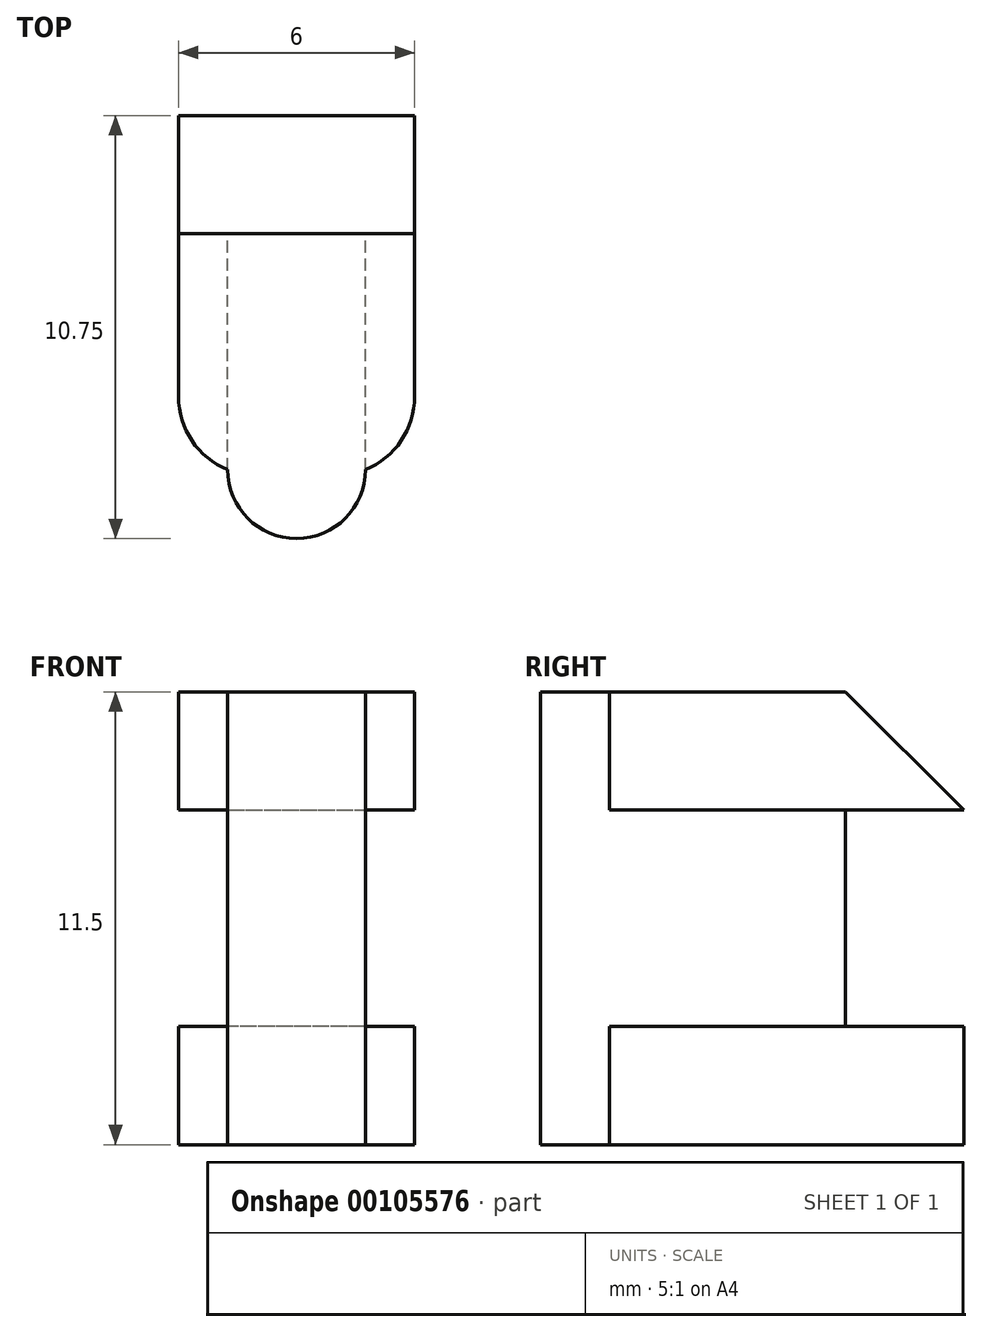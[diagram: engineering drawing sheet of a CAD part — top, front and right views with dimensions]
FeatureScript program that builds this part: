
annotation { "Feature Type Name" : "Feature", "Feature Type Description" : "" }
export const myFeature = defineFeature(function(context is Context, id is Id, definition is map)
    precondition{}
    {
        {
            var Q0;
            Q0=qCreatedBy(makeId("Front.planeOp"),FACE);
            var sketch = newSketch(context, id + "F0", { "sketchPlane" : qUnion([Q0])});
            skLineSegment(sketch, "E0.bottom", {"start": v(3, -1.5) * mm, "end": v(-3, -1.5) * mm});
            skLineSegment(sketch, "E0.top", {"start": v(3, 1.5) * mm, "end": v(-3, 1.5) * mm});
            skLineSegment(sketch, "E0.left", {"start": v(3, -1.5) * mm, "end": v(3, 1.5) * mm});
            skLineSegment(sketch, "E0.right", {"start": v(-3, -1.5) * mm, "end": v(-3, 1.5) * mm});
            skPoint(sketch, "E0.middle", {"position": v(0, 0) * mm});
            skLineSegment(sketch, "E1.bottom", {"start": v(1.75, -1.5) * mm, "end": v(-1.75, -1.5) * mm});
            skLineSegment(sketch, "E1.top", {"start": v(1.75, -7) * mm, "end": v(-1.75, -7) * mm});
            skLineSegment(sketch, "E1.left", {"start": v(1.75, -1.5) * mm, "end": v(1.75, -7) * mm});
            skLineSegment(sketch, "E1.right", {"start": v(-1.75, -1.5) * mm, "end": v(-1.75, -7) * mm});
            skPoint(sketch, "E1.middle", {"position": v(0, -4.25) * mm});
            skPoint(sketch, "E1.middle.positionSnap0", {"position": v(0, -1.5) * mm});
            skPoint(sketch, "E1.centerSnap0", {"position": v(0, -1.5) * mm});
            skLineSegment(sketch, "E2.bottom", {"start": v(-3, -7) * mm, "end": v(3, -7) * mm});
            skLineSegment(sketch, "E2.top", {"start": v(-3, -10) * mm, "end": v(3, -10) * mm});
            skLineSegment(sketch, "E2.left", {"start": v(-3, -7) * mm, "end": v(-3, -10) * mm});
            skLineSegment(sketch, "E2.right", {"start": v(3, -7) * mm, "end": v(3, -10) * mm});
            skPoint(sketch, "E2.middle", {"position": v(0, -8.5) * mm});
            skPoint(sketch, "E2.cornerSnap0", {"position": v(0, -7) * mm});
            skSolve(sketch);
        }
        {
            var Q0;
            Q0 = qSketchRegion(id + "F0", true);
            extrude(context, id + "F1", {"entities" : qUnion([Q0]), "depth" : 6 * mm});
        }
        {
            var Q0;
            Q0=makeQuery(id+"F1.opExtrude","CAP_FACE",FACE,{"disambiguationData":[OSD([sQuery(id+"F0.wireOp",EDGE,"E0.bottom"),sQuery(id+"F0.wireOp",EDGE,"E0.top"),sQuery(id+"F0.wireOp",EDGE,"E0.left"),sQuery(id+"F0.wireOp",EDGE,"E0.right"),sQuery(id+"F0.wireOp",EDGE,"E1.left"),sQuery(id+"F0.wireOp",EDGE,"E1.right"),sQuery(id+"F0.wireOp",EDGE,"E2.bottom"),sQuery(id+"F0.wireOp",EDGE,"E2.top"),sQuery(id+"F0.wireOp",EDGE,"E2.left"),sQuery(id+"F0.wireOp",EDGE,"E2.right")])],"isStart":false});
            var sketch = newSketch(context, id + "F2", { "sketchPlane" : qUnion([Q0])});
            skLineSegment(sketch, "E3.bottom", {"start": v(-1.75, 1.5) * mm, "end": v(0, 1.5) * mm});
            skLineSegment(sketch, "E3.top", {"start": v(-1.75, -10) * mm, "end": v(0, -10) * mm});
            skLineSegment(sketch, "E3.left", {"start": v(-1.75, 1.5) * mm, "end": v(-1.75, -10) * mm});
            skLineSegment(sketch, "E3.right", {"start": v(0, 1.5) * mm, "end": v(0, -10) * mm});
            skSolve(sketch);
        }
        {
            var Q0;
            Q0 = qSketchRegion(id + "F2", true);
            var Q1;
            Q1=sQuery(id+"F2.wireOp",EDGE,"E3.right");
            revolve(context, id + "F3", {"operationType" : NewBodyOperationType.ADD, "entities" : qUnion([Q0]), "axis" : qUnion([Q1]), "revolveType" : RevolveType.FULL});
        }
        {
            var Q0;
            Q0=makeQuery(id+"F1.opExtrude","CAP_EDGE",EDGE,{"disambiguationData":[OSD([sQuery(id+"F0.wireOp",EDGE,"E0.left")])],"isStart":false});
            var Q1;
            Q1=makeQuery(id+"F1.opExtrude","CAP_EDGE",EDGE,{"disambiguationData":[OSD([sQuery(id+"F0.wireOp",EDGE,"E0.right")])],"isStart":false});
            var Q2;
            Q2=makeQuery(id+"F1.opExtrude","CAP_EDGE",EDGE,{"disambiguationData":[OSD([sQuery(id+"F0.wireOp",EDGE,"E2.right")])],"isStart":false});
            var Q3;
            Q3=makeQuery(id+"F1.opExtrude","CAP_EDGE",EDGE,{"disambiguationData":[OSD([sQuery(id+"F0.wireOp",EDGE,"E2.left")])],"isStart":false});
            fillet(context, id + "F4", {"entities" : qUnion([Q0, Q1, Q2, Q3]), "radius" : 2 * mm, "tangentPropagation" : true, "allowEdgeOverflow" : false});
        }
        {
            var Q0;
            Q0=makeQuery(id+"F1.opExtrude","CAP_FACE",FACE,{"disambiguationData":[OSD([sQuery(id+"F0.wireOp",EDGE,"E0.bottom"),sQuery(id+"F0.wireOp",EDGE,"E0.top"),sQuery(id+"F0.wireOp",EDGE,"E0.left"),sQuery(id+"F0.wireOp",EDGE,"E0.right"),sQuery(id+"F0.wireOp",EDGE,"E1.left"),sQuery(id+"F0.wireOp",EDGE,"E1.right"),sQuery(id+"F0.wireOp",EDGE,"E2.bottom"),sQuery(id+"F0.wireOp",EDGE,"E2.top"),sQuery(id+"F0.wireOp",EDGE,"E2.left"),sQuery(id+"F0.wireOp",EDGE,"E2.right")])],"isStart":true});
            var sketch = newSketch(context, id + "F5", { "sketchPlane" : qUnion([Q0])});
            skLineSegment(sketch, "E4.bottom", {"start": v(3, -1.5) * mm, "end": v(-3, -1.5) * mm});
            skLineSegment(sketch, "E4.top", {"start": v(3, 1.5) * mm, "end": v(-3, 1.5) * mm});
            skLineSegment(sketch, "E4.left", {"start": v(3, -1.5) * mm, "end": v(3, 1.5) * mm});
            skLineSegment(sketch, "E4.right", {"start": v(-3, -1.5) * mm, "end": v(-3, 1.5) * mm});
            skPoint(sketch, "E4.middle", {"position": v(0, 0) * mm});
            skLineSegment(sketch, "E5.bottom", {"start": v(-3, -7) * mm, "end": v(3, -7) * mm});
            skLineSegment(sketch, "E5.top", {"start": v(-3, -10) * mm, "end": v(3, -10) * mm});
            skLineSegment(sketch, "E5.left", {"start": v(-3, -7) * mm, "end": v(-3, -10) * mm});
            skLineSegment(sketch, "E5.right", {"start": v(3, -7) * mm, "end": v(3, -10) * mm});
            skSolve(sketch);
        }
        {
            var Q0;
            Q0 = qSketchRegion(id + "F5", true);
            extrude(context, id + "F6", {"entities" : qUnion([Q0]), "operationType" : NewBodyOperationType.ADD, "depth" : 3 * mm});
        }
        {
            var Q0;
            Q0=makeQuery(id+"F6.boolean.opBoolean","MERGE",FACE,{"derivedFrom":[makeQuery(id+"F1.opExtrude","SWEPT_FACE",FACE,{"disambiguationData":[OSD([sQuery(id+"F0.wireOp",EDGE,"E0.left")])]}),makeQuery(id+"F6.opExtrude","SWEPT_FACE",FACE,{"disambiguationData":[OSD([sQuery(id+"F5.wireOp",EDGE,"E4.right")])]})]});
            var sketch = newSketch(context, id + "F7", { "sketchPlane" : qUnion([Q0])});
            skLineSegment(sketch, "E6", {"start": v(3, -1.5) * mm, "end": v(0, 1.5) * mm});
            skLineSegment(sketch, "E7", {"start": v(0, 1.5) * mm, "end": v(3, 1.5) * mm});
            skLineSegment(sketch, "E8", {"start": v(3, 1.5) * mm, "end": v(3, -1.5) * mm});
            skSolve(sketch);
        }
        {
            var Q0;
            Q0=makeQuery(id+"F7.imprint","IMPRINT",FACE,{"disambiguationData":[TD([[makeQuery(id+"F7.imprint","IMPRINT",EDGE,{"derivedFrom":sQuery(id+"F7.wireOp",EDGE,"E6")}),-1.0]])]});
            extrude(context, id + "F8", {"entities" : qUnion([Q0]), "operationType" : NewBodyOperationType.REMOVE, "oppositeDirection" : true, "depth" : 25 * mm});
        }
    });
